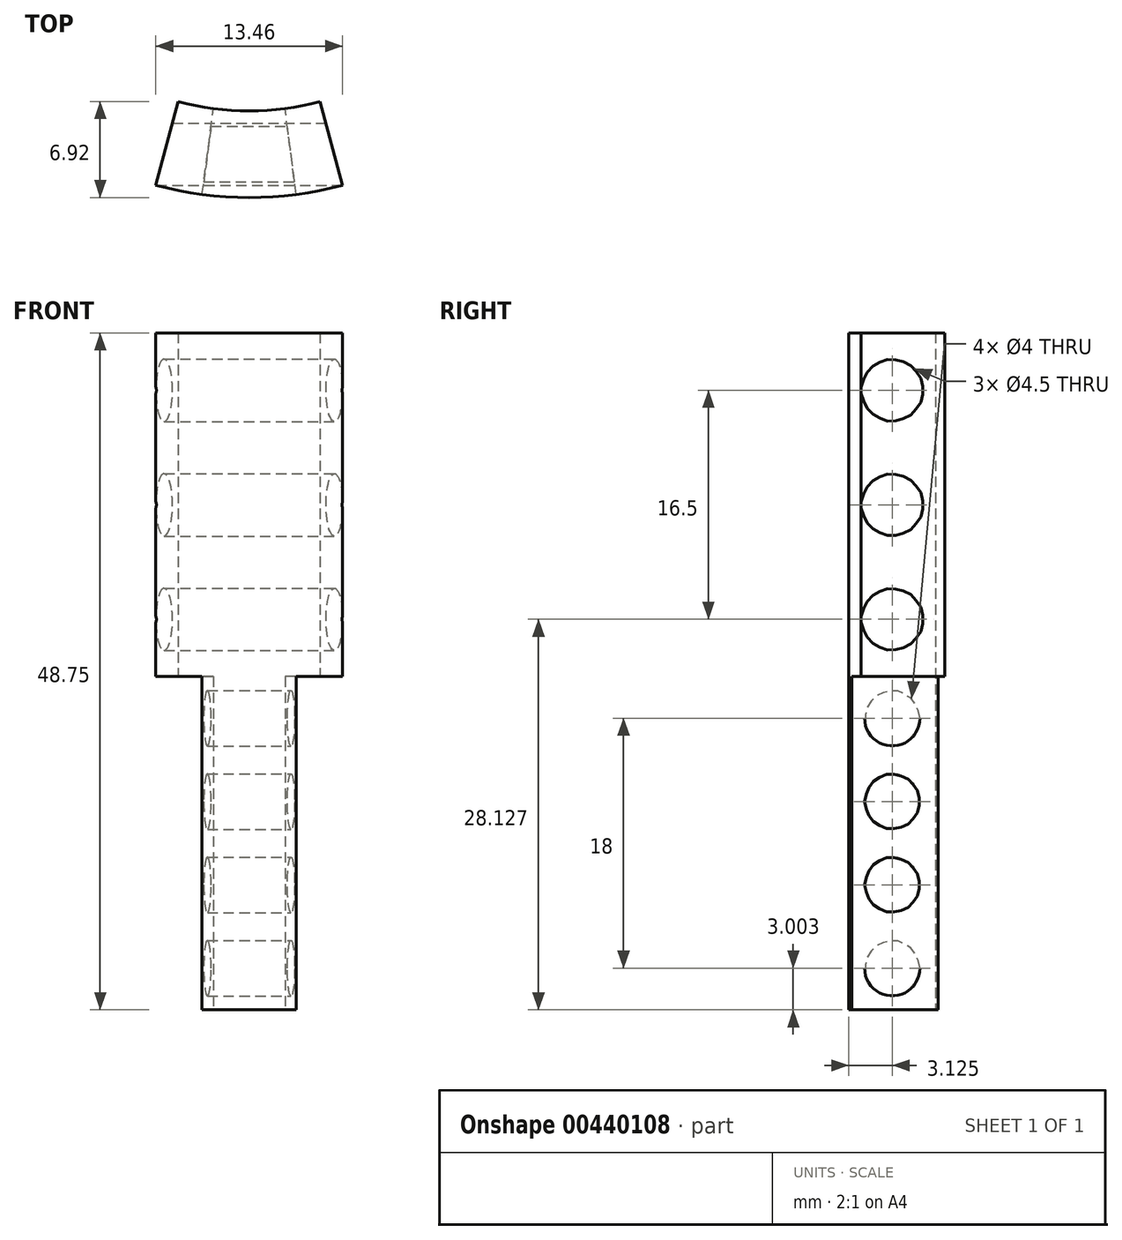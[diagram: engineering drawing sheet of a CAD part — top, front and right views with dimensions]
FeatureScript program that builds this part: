
annotation { "Feature Type Name" : "Feature", "Feature Type Description" : "" }
export const myFeature = defineFeature(function(context is Context, id is Id, definition is map)
    precondition{}
    {
        {
            var Q0;
            Q0=qCreatedBy(makeId("Right.planeOp"),FACE);
            var sketch = newSketch(context, id + "F0", { "sketchPlane" : qUnion([Q0])});
            skLineSegment(sketch, "E0", {"start": v(0, 0) * mm, "end": v(26.5, 0) * mm, "construction": true});
            skLineSegment(sketch, "E1", {"start": v(0, 0) * mm, "end": v(0, 126) * mm, "construction": true});
            skLineSegment(sketch, "E2", {"start": v(26.5, 0) * mm, "end": v(28.5, 0) * mm, "construction": true});
            skLineSegment(sketch, "E3", {"start": v(19.75, 0) * mm, "end": v(19.75, 126) * mm, "construction": true});
            skLineSegment(sketch, "E4", {"start": v(26.5, 0) * mm, "end": v(26.5, 126) * mm, "construction": true});
            skLineSegment(sketch, "E5", {"start": v(28.5, 0) * mm, "end": v(28.5, 126) * mm, "construction": true});
            skLineSegment(sketch, "E6", {"start": v(28.5, 0) * mm, "end": v(34.75, 0) * mm, "construction": true});
            skLineSegment(sketch, "E7", {"start": v(34.75, 0) * mm, "end": v(36.75, 0) * mm, "construction": true});
            skLineSegment(sketch, "E8", {"start": v(34.75, 0) * mm, "end": v(34.75, 76) * mm, "construction": true});
            skLineSegment(sketch, "E9", {"start": v(36.75, 0) * mm, "end": v(36.75, 76) * mm, "construction": true});
            skLineSegment(sketch, "E10", {"start": v(0, 76) * mm, "end": v(34.75, 76) * mm, "construction": true});
            skLineSegment(sketch, "E11", {"start": v(34.75, 76) * mm, "end": v(36.75, 76) * mm, "construction": true});
            skLineSegment(sketch, "E12", {"start": v(28.5, 126) * mm, "end": v(36.75, 76) * mm});
            skLineSegment(sketch, "E13", {"start": v(26.5, 126) * mm, "end": v(34.75, 76) * mm});
            skLineSegment(sketch, "E14", {"start": v(34.75, 76) * mm, "end": v(34.75, 0) * mm});
            skLineSegment(sketch, "E15", {"start": v(36.75, 76) * mm, "end": v(36.75, 0) * mm});
            skLineSegment(sketch, "E16", {"start": v(26.5, 126) * mm, "end": v(28.5, 126) * mm});
            skLineSegment(sketch, "E17", {"start": v(34.75, 0) * mm, "end": v(36.75, 0) * mm});
            skLineSegment(sketch, "E18.MirrorCS", {"start": v(-34.75, 0) * mm, "end": v(-36.75, 0) * mm});
            skLineSegment(sketch, "E19.MirrorCS", {"start": v(-34.75, 0) * mm, "end": v(-36.75, 0) * mm, "construction": true});
            skLineSegment(sketch, "E20.MirrorCS", {"start": v(-26.5, 0) * mm, "end": v(-28.5, 0) * mm, "construction": true});
            skLineSegment(sketch, "E21.MirrorCS", {"start": v(-26.5, 126) * mm, "end": v(-28.5, 126) * mm});
            skLineSegment(sketch, "E22.MirrorCS", {"start": v(-28.5, 0) * mm, "end": v(-34.75, 0) * mm, "construction": true});
            skLineSegment(sketch, "E23.MirrorCS", {"start": v(-36.75, 76) * mm, "end": v(-36.75, 0) * mm});
            skLineSegment(sketch, "E24.MirrorCS", {"start": v(-28.5, 0) * mm, "end": v(-28.5, 126) * mm, "construction": true});
            skLineSegment(sketch, "E25.MirrorCS", {"start": v(0, 0) * mm, "end": v(-26.5, 0) * mm, "construction": true});
            skLineSegment(sketch, "E26.MirrorCS", {"start": v(-34.75, 76) * mm, "end": v(-34.75, 0) * mm});
            skLineSegment(sketch, "E27.MirrorCS", {"start": v(-26.5, 0) * mm, "end": v(-26.5, 126) * mm, "construction": true});
            skLineSegment(sketch, "E28.MirrorCS", {"start": v(-26.5, 126) * mm, "end": v(-34.75, 76) * mm});
            skLineSegment(sketch, "E29.MirrorCS", {"start": v(-19.75, 0) * mm, "end": v(-19.75, 126) * mm, "construction": true});
            skLineSegment(sketch, "E30.MirrorCS", {"start": v(-34.75, 0) * mm, "end": v(-34.75, 76) * mm, "construction": true});
            skLineSegment(sketch, "E31.MirrorCS", {"start": v(-36.75, 0) * mm, "end": v(-36.75, 76) * mm, "construction": true});
            skLineSegment(sketch, "E32.MirrorCS", {"start": v(0, 76) * mm, "end": v(-34.75, 76) * mm, "construction": true});
            skLineSegment(sketch, "E33.MirrorCS", {"start": v(-28.5, 126) * mm, "end": v(-36.75, 76) * mm});
            skLineSegment(sketch, "E34", {"start": v(-26.5, 126) * mm, "end": v(-26.5, 101) * mm});
            skPoint(sketch, "E34.endSnap0", {"position": v(-30.63, 101) * mm});
            skLineSegment(sketch, "E35", {"start": v(-26.5, 101) * mm, "end": v(-30.63, 101) * mm});
            skLineSegment(sketch, "E36.bottom", {"start": v(-34.75, 61.36) * mm, "end": v(-28.5, 61.36) * mm});
            skLineSegment(sketch, "E36.top", {"start": v(-34.75, 36.61) * mm, "end": v(-28.5, 36.61) * mm});
            skLineSegment(sketch, "E36.left", {"start": v(-34.75, 61.36) * mm, "end": v(-34.75, 36.61) * mm});
            skLineSegment(sketch, "E36.right", {"start": v(-28.5, 61.36) * mm, "end": v(-28.5, 36.61) * mm});
            skCircle(sketch, "E37", {"center": v(-31.63, 48.99) * mm, "radius": 2.25 * mm});
            skPoint(sketch, "E37.centerSnap0", {"position": v(-31.63, 61.36) * mm});
            skPoint(sketch, "E37.centerSnap1", {"position": v(-34.75, 48.99) * mm});
            skCircle(sketch, "E38", {"center": v(-31.63, 57.24) * mm, "radius": 2.25 * mm});
            skCircle(sketch, "E39", {"center": v(-31.63, 40.74) * mm, "radius": 2.25 * mm});
            skPoint(sketch, "E39.centerSnap0", {"position": v(-31.63, 36.61) * mm});
            skLineSegment(sketch, "E40.top", {"start": v(-34.75, 12.61) * mm, "end": v(-28.5, 12.61) * mm});
            skLineSegment(sketch, "E40.left", {"start": v(-34.75, 36.61) * mm, "end": v(-34.75, 12.61) * mm});
            skLineSegment(sketch, "E40.right", {"start": v(-28.5, 36.61) * mm, "end": v(-28.5, 12.61) * mm});
            skCircle(sketch, "E41", {"center": v(-31.63, 33.61) * mm, "radius": 2 * mm});
            skCircle(sketch, "E42.1.0.0", {"center": v(-31.63, 27.61) * mm, "radius": 2 * mm});
            skCircle(sketch, "E42.2.0.0", {"center": v(-31.63, 21.61) * mm, "radius": 2 * mm});
            skCircle(sketch, "E42.3.0.0", {"center": v(-31.63, 15.61) * mm, "radius": 2 * mm});
            skLineSegment(sketch, "E42.direction1", {"start": v(-31.63, 33.61) * mm, "end": v(-31.63, 27.61) * mm, "construction": true});
            skLineSegment(sketch, "E43", {"start": v(-31.63, 36.61) * mm, "end": v(-31.63, 12.61) * mm, "construction": true});
            skLineSegment(sketch, "E44", {"start": v(-27.5, 0) * mm, "end": v(-27.5, 76) * mm, "construction": true});
            skLineSegment(sketch, "E45.bottom", {"start": v(-26, 61.36) * mm, "end": v(-19.75, 61.36) * mm});
            skLineSegment(sketch, "E45.top", {"start": v(-26, 36.61) * mm, "end": v(-19.75, 36.61) * mm});
            skLineSegment(sketch, "E45.left", {"start": v(-26, 61.36) * mm, "end": v(-26, 36.61) * mm});
            skLineSegment(sketch, "E45.right", {"start": v(-19.75, 61.36) * mm, "end": v(-19.75, 36.61) * mm});
            skCircle(sketch, "E46", {"center": v(-22.87, 48.99) * mm, "radius": 2.25 * mm});
            skPoint(sketch, "E46.centerSnap0", {"position": v(-22.87, 61.36) * mm});
            skCircle(sketch, "E47", {"center": v(-22.87, 57.24) * mm, "radius": 2.25 * mm});
            skCircle(sketch, "E48", {"center": v(-22.87, 40.74) * mm, "radius": 2.25 * mm});
            skPoint(sketch, "E48.centerSnap0", {"position": v(-22.87, 36.61) * mm});
            skLineSegment(sketch, "E49.top", {"start": v(-26, 12.61) * mm, "end": v(-19.75, 12.61) * mm});
            skLineSegment(sketch, "E49.left", {"start": v(-26, 36.61) * mm, "end": v(-26, 12.61) * mm});
            skLineSegment(sketch, "E49.right", {"start": v(-19.75, 36.61) * mm, "end": v(-19.75, 12.61) * mm});
            skCircle(sketch, "E50", {"center": v(-22.87, 33.61) * mm, "radius": 2 * mm});
            skCircle(sketch, "E51.1.0.0", {"center": v(-22.87, 27.61) * mm, "radius": 2 * mm});
            skCircle(sketch, "E51.2.0.0", {"center": v(-22.87, 21.61) * mm, "radius": 2 * mm});
            skCircle(sketch, "E51.3.0.0", {"center": v(-22.87, 15.61) * mm, "radius": 2 * mm});
            skLineSegment(sketch, "E51.direction1", {"start": v(-22.87, 33.61) * mm, "end": v(-22.87, 27.61) * mm, "construction": true});
            skLineSegment(sketch, "E52", {"start": v(-22.87, 36.61) * mm, "end": v(-22.87, 12.61) * mm, "construction": true});
            skSolve(sketch);
        }
        {
            var Q0;
            Q0=makeQuery(id+"F0.imprint","IMPRINT",FACE,{"disambiguationData":[TD([[makeQuery(id+"F0.imprint","IMPRINT",EDGE,{"derivedFrom":sQuery(id+"F0.wireOp",EDGE,"E45.bottom")}),-1.0]])]});
            var Q1;
            Q1=makeQuery(id+"F0.imprint","IMPRINT",FACE,{"disambiguationData":[TD([[makeQuery(id+"F0.imprint","IMPRINT",EDGE,{"derivedFrom":sQuery(id+"F0.wireOp",EDGE,"E47")}),1.0]])]});
            var Q2;
            Q2=makeQuery(id+"F0.imprint","IMPRINT",FACE,{"disambiguationData":[TD([[makeQuery(id+"F0.imprint","IMPRINT",EDGE,{"derivedFrom":sQuery(id+"F0.wireOp",EDGE,"E46")}),1.0]])]});
            var Q3;
            Q3=makeQuery(id+"F0.imprint","IMPRINT",FACE,{"disambiguationData":[TD([[makeQuery(id+"F0.imprint","IMPRINT",EDGE,{"derivedFrom":sQuery(id+"F0.wireOp",EDGE,"E48")}),1.0]])]});
            var Q4;
            Q4=sQuery(id+"F0.wireOp",EDGE,"E1");
            revolve(context, id + "F1", {"entities" : qUnion([Q0, Q1, Q2, Q3]), "axis" : qUnion([Q4]), "revolveType" : RevolveType.SYMMETRIC, "angle" : 30 * degree});
        }
        {
            var Q0;
            Q0=makeQuery(id+"F0.imprint","IMPRINT",FACE,{"disambiguationData":[TD([[makeQuery(id+"F0.imprint","IMPRINT",EDGE,{"derivedFrom":sQuery(id+"F0.wireOp",EDGE,"E47")}),1.0]])]});
            var Q1;
            Q1=makeQuery(id+"F0.imprint","IMPRINT",FACE,{"disambiguationData":[TD([[makeQuery(id+"F0.imprint","IMPRINT",EDGE,{"derivedFrom":sQuery(id+"F0.wireOp",EDGE,"E46")}),1.0]])]});
            var Q2;
            Q2=makeQuery(id+"F0.imprint","IMPRINT",FACE,{"disambiguationData":[TD([[makeQuery(id+"F0.imprint","IMPRINT",EDGE,{"derivedFrom":sQuery(id+"F0.wireOp",EDGE,"E48")}),1.0]])]});
            extrude(context, id + "F2", {"entities" : qUnion([Q0, Q1, Q2]), "operationType" : NewBodyOperationType.REMOVE, "endBound" : BoundingType.SYMMETRIC, "oppositeDirection" : true, "depth" : 25 * mm, "offsetDistance" : 25 * mm});
        }
        {
            var Q0;
            Q0=makeQuery(id+"F0.imprint","IMPRINT",FACE,{"disambiguationData":[TD([[makeQuery(id+"F0.imprint","IMPRINT",EDGE,{"derivedFrom":sQuery(id+"F0.wireOp",EDGE,"E45.top")}),-1.0]])]});
            var Q1;
            Q1=makeQuery(id+"F0.imprint","IMPRINT",FACE,{"disambiguationData":[TD([[makeQuery(id+"F0.imprint","IMPRINT",EDGE,{"derivedFrom":sQuery(id+"F0.wireOp",EDGE,"E50")}),1.0]])]});
            var Q2;
            Q2=makeQuery(id+"F0.imprint","IMPRINT",FACE,{"disambiguationData":[TD([[makeQuery(id+"F0.imprint","IMPRINT",EDGE,{"derivedFrom":sQuery(id+"F0.wireOp",EDGE,"E51.1.0.0")}),1.0]])]});
            var Q3;
            Q3=makeQuery(id+"F0.imprint","IMPRINT",FACE,{"disambiguationData":[TD([[makeQuery(id+"F0.imprint","IMPRINT",EDGE,{"derivedFrom":sQuery(id+"F0.wireOp",EDGE,"E51.2.0.0")}),1.0]])]});
            var Q4;
            Q4=makeQuery(id+"F0.imprint","IMPRINT",FACE,{"disambiguationData":[TD([[makeQuery(id+"F0.imprint","IMPRINT",EDGE,{"derivedFrom":sQuery(id+"F0.wireOp",EDGE,"E51.3.0.0")}),1.0]])]});
            var Q5;
            Q5=sQuery(id+"F0.wireOp",EDGE,"E1");
            revolve(context, id + "F3", {"operationType" : NewBodyOperationType.ADD, "entities" : qUnion([Q0, Q1, Q2, Q3, Q4]), "axis" : qUnion([Q5]), "revolveType" : RevolveType.SYMMETRIC, "angle" : 15 * degree});
        }
        {
            var Q0;
            Q0=makeQuery(id+"F0.imprint","IMPRINT",FACE,{"disambiguationData":[TD([[makeQuery(id+"F0.imprint","IMPRINT",EDGE,{"derivedFrom":sQuery(id+"F0.wireOp",EDGE,"E50")}),1.0]])]});
            var Q1;
            Q1=makeQuery(id+"F0.imprint","IMPRINT",FACE,{"disambiguationData":[TD([[makeQuery(id+"F0.imprint","IMPRINT",EDGE,{"derivedFrom":sQuery(id+"F0.wireOp",EDGE,"E51.1.0.0")}),1.0]])]});
            var Q2;
            Q2=makeQuery(id+"F0.imprint","IMPRINT",FACE,{"disambiguationData":[TD([[makeQuery(id+"F0.imprint","IMPRINT",EDGE,{"derivedFrom":sQuery(id+"F0.wireOp",EDGE,"E51.2.0.0")}),1.0]])]});
            var Q3;
            Q3=makeQuery(id+"F0.imprint","IMPRINT",FACE,{"disambiguationData":[TD([[makeQuery(id+"F0.imprint","IMPRINT",EDGE,{"derivedFrom":sQuery(id+"F0.wireOp",EDGE,"E51.3.0.0")}),1.0]])]});
            extrude(context, id + "F4", {"entities" : qUnion([Q0, Q1, Q2, Q3]), "operationType" : NewBodyOperationType.REMOVE, "endBound" : BoundingType.SYMMETRIC, "oppositeDirection" : true, "depth" : 10 * mm, "offsetDistance" : 25 * mm});
        }
    });
